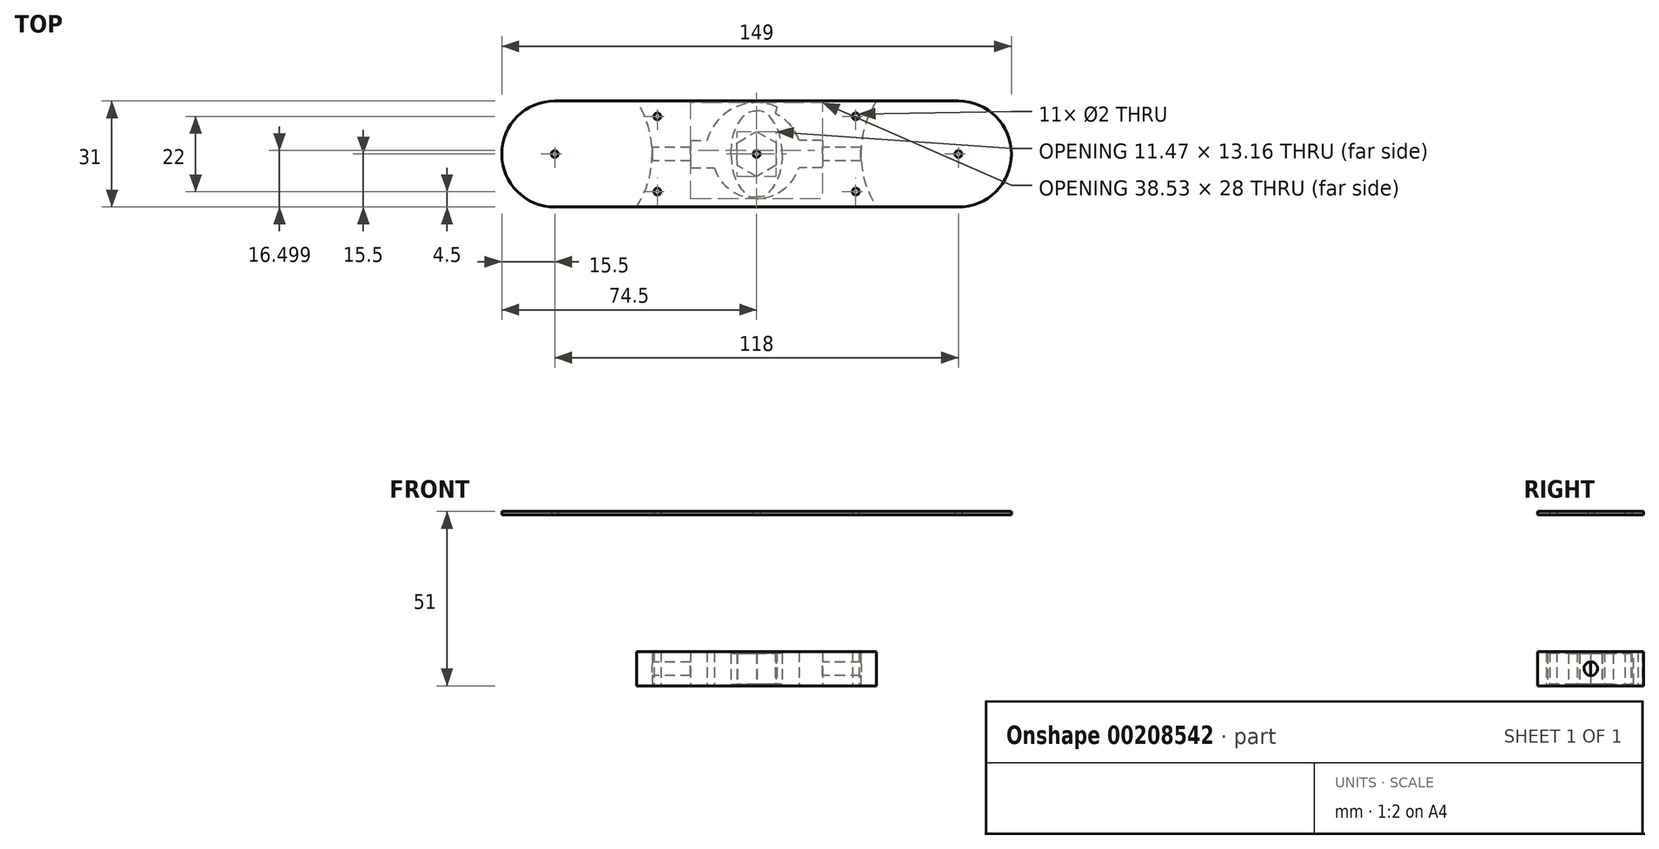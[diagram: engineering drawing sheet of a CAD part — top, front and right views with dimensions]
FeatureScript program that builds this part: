
annotation { "Feature Type Name" : "Feature", "Feature Type Description" : "" }
export const myFeature = defineFeature(function(context is Context, id is Id, definition is map)
    precondition{}
    {
        {
            var Q0;
            Q0=qCreatedBy(makeId("Top.planeOp"),FACE);
            var sketch = newSketch(context, id + "F0", { "sketchPlane" : qUnion([Q0])});
            skCircle(sketch, "E0", {"center": v(59, 0) * mm, "radius": 27.5 * mm});
            skCircle(sketch, "E1", {"center": v(-59, 0) * mm, "radius": 27.5 * mm});
            skCircle(sketch, "E2.0", {"center": v(59, 0) * mm, "radius": 28.5 * mm});
            skCircle(sketch, "E3.0", {"center": v(-59, 0) * mm, "radius": 28.5 * mm});
            skCircle(sketch, "E4", {"center": v(0, 0) * mm, "radius": 13 * mm});
            skCircle(sketch, "E5", {"center": v(59, 0) * mm, "radius": 15.5 * mm});
            skCircle(sketch, "E6", {"center": v(-59, 0) * mm, "radius": 15.5 * mm});
            skLineSegment(sketch, "E7", {"start": v(59.04, 15.5) * mm, "end": v(-59, 15.5) * mm});
            skLineSegment(sketch, "E8", {"start": v(-59.05, -15.5) * mm, "end": v(59, -15.5) * mm});
            skCircle(sketch, "E9", {"center": v(29, 11) * mm, "radius": 1 * mm});
            skCircle(sketch, "E10.MirrorC", {"center": v(-29, 11) * mm, "radius": 1 * mm});
            skCircle(sketch, "E11.MirrorC", {"center": v(29, -11) * mm, "radius": 1 * mm});
            skCircle(sketch, "E12.MirrorC", {"center": v(-29, -11) * mm, "radius": 1 * mm});
            skLineSegment(sketch, "E13.bottom", {"start": v(19.26, 4) * mm, "end": v(9.26, 4) * mm});
            skLineSegment(sketch, "E13.top", {"start": v(19.26, -4) * mm, "end": v(9.26, -4) * mm});
            skLineSegment(sketch, "E13.left", {"start": v(19.26, 4) * mm, "end": v(19.26, -4) * mm});
            skLineSegment(sketch, "E13.right", {"start": v(9.26, 4) * mm, "end": v(9.26, -4) * mm});
            skLineSegment(sketch, "E14.MirrorCS", {"start": v(-19.26, 4) * mm, "end": v(-19.26, -4) * mm});
            skLineSegment(sketch, "E15.MirrorCS", {"start": v(-19.26, 4) * mm, "end": v(-9.26, 4) * mm});
            skLineSegment(sketch, "E16.MirrorCS", {"start": v(-9.26, 4) * mm, "end": v(-9.26, -4) * mm});
            skLineSegment(sketch, "E17.MirrorCS", {"start": v(-19.26, -4) * mm, "end": v(-9.26, -4) * mm});
            skCircle(sketch, "E18.0", {"center": v(0, 0) * mm, "radius": 15 * mm});
            skLineSegment(sketch, "E19", {"start": v(5.95, 13.77) * mm, "end": v(5.43, 11.81) * mm});
            skCircle(sketch, "E20.cCircle", {"center": v(0, 0) * mm, "radius": 5.7 * mm, "construction": true});
            skLineSegment(sketch, "E20.0", {"start": v(-0.07, 6.58) * mm, "end": v(5.66, 3.35) * mm});
            skLineSegment(sketch, "E20.1", {"start": v(5.66, 3.35) * mm, "end": v(5.74, -3.23) * mm});
            skLineSegment(sketch, "E20.2", {"start": v(5.74, -3.23) * mm, "end": v(0.07, -6.58) * mm});
            skLineSegment(sketch, "E20.3", {"start": v(0.07, -6.58) * mm, "end": v(-5.66, -3.35) * mm});
            skLineSegment(sketch, "E20.4", {"start": v(-5.66, -3.35) * mm, "end": v(-5.74, 3.23) * mm});
            skLineSegment(sketch, "E20.5", {"start": v(-5.74, 3.23) * mm, "end": v(-0.07, 6.58) * mm});
            skPoint(sketch, "E20.0.midPoint", {"position": v(2.8, 4.97) * mm});
            skCircle(sketch, "E21", {"center": v(-59, 0) * mm, "radius": 1 * mm});
            skCircle(sketch, "E22", {"center": v(59, 0) * mm, "radius": 1 * mm});
            skCircle(sketch, "E23", {"center": v(0, 0) * mm, "radius": 1 * mm});
            skLineSegment(sketch, "E24", {"start": v(-73.26, 28.93) * mm, "end": v(99.1, 13.06) * mm});
            skLineSegment(sketch, "E25", {"start": v(-95.04, -13.9) * mm, "end": v(98.15, -31.1) * mm});
            skLineSegment(sketch, "E26", {"start": v(32.84, 0) * mm, "end": v(29.84, 0) * mm});
            skLineSegment(sketch, "E27.1.0", {"start": v(33.37, -5.27) * mm, "end": v(30.43, -5.87) * mm});
            skLineSegment(sketch, "E27.2.0", {"start": v(34.96, -10.32) * mm, "end": v(32.2, -11.5) * mm});
            skLineSegment(sketch, "E28.2.3.0", {"start": v(37.53, -14.95) * mm, "end": v(35.06, -16.66) * mm});
            skLineSegment(sketch, "E28.2.4.0", {"start": v(40.97, -18.96) * mm, "end": v(38.9, -21.14) * mm});
            skLineSegment(sketch, "E28.2.5.0", {"start": v(45.16, -22.2) * mm, "end": v(43.57, -24.75) * mm});
            skLineSegment(sketch, "E28.2.6.0", {"start": v(49.91, -24.53) * mm, "end": v(48.87, -27.35) * mm});
            skLineSegment(sketch, "E28.2.7.0", {"start": v(55.04, -25.86) * mm, "end": v(54.58, -28.83) * mm});
            skLineSegment(sketch, "E28.2.8.0", {"start": v(60.33, -26.13) * mm, "end": v(60.48, -29.13) * mm});
            skLineSegment(sketch, "E28.2.9.0", {"start": v(65.56, -25.33) * mm, "end": v(66.3, -28.23) * mm});
            skLineSegment(sketch, "E28.2.10.0", {"start": v(70.52, -23.49) * mm, "end": v(71.84, -26.18) * mm});
            skLineSegment(sketch, "E28.2.11.0", {"start": v(75.01, -20.69) * mm, "end": v(76.85, -23.06) * mm});
            skLineSegment(sketch, "E28.2.12.0", {"start": v(78.85, -17.04) * mm, "end": v(81.13, -19) * mm});
            skLineSegment(sketch, "E28.2.13.0", {"start": v(81.88, -12.7) * mm, "end": v(84.5, -14.15) * mm});
            skLineSegment(sketch, "E28.2.14.0", {"start": v(83.96, -7.83) * mm, "end": v(86.83, -8.73) * mm});
            skLineSegment(sketch, "E28.2.15.0", {"start": v(85.03, -2.65) * mm, "end": v(88.01, -2.95) * mm});
            skLineSegment(sketch, "E28.2.16.0", {"start": v(85.03, 2.65) * mm, "end": v(88.01, 2.95) * mm});
            skLineSegment(sketch, "E28.2.17.0", {"start": v(83.96, 7.83) * mm, "end": v(86.83, 8.73) * mm});
            skLineSegment(sketch, "E28.2.18.0", {"start": v(81.88, 12.7) * mm, "end": v(84.5, 14.15) * mm});
            skLineSegment(sketch, "E28.2.19.0", {"start": v(78.85, 17.04) * mm, "end": v(81.13, 19) * mm});
            skLineSegment(sketch, "E28.2.20.0", {"start": v(75.01, 20.69) * mm, "end": v(76.85, 23.06) * mm});
            skLineSegment(sketch, "E28.2.21.0", {"start": v(70.52, 23.49) * mm, "end": v(71.84, 26.18) * mm});
            skLineSegment(sketch, "E28.2.22.0", {"start": v(65.56, 25.33) * mm, "end": v(66.3, 28.23) * mm});
            skLineSegment(sketch, "E28.2.23.0", {"start": v(60.33, 26.13) * mm, "end": v(60.48, 29.13) * mm});
            skLineSegment(sketch, "E28.2.24.0", {"start": v(55.04, 25.86) * mm, "end": v(54.58, 28.83) * mm});
            skLineSegment(sketch, "E28.2.25.0", {"start": v(49.91, 24.53) * mm, "end": v(48.87, 27.35) * mm});
            skLineSegment(sketch, "E28.2.26.0", {"start": v(45.16, 22.2) * mm, "end": v(43.57, 24.75) * mm});
            skLineSegment(sketch, "E28.2.27.0", {"start": v(40.97, 18.96) * mm, "end": v(38.9, 21.14) * mm});
            skLineSegment(sketch, "E29", {"start": v(-33.37, 0) * mm, "end": v(-30.37, 0) * mm});
            skLineSegment(sketch, "E30.1.0", {"start": v(-33.9, 5.16) * mm, "end": v(-30.95, 5.76) * mm});
            skLineSegment(sketch, "E30.2.0", {"start": v(-35.44, 10.1) * mm, "end": v(-32.69, 11.3) * mm});
            skLineSegment(sketch, "E31.1.3.0", {"start": v(-37.96, 14.64) * mm, "end": v(-35.5, 16.36) * mm});
            skLineSegment(sketch, "E31.1.4.0", {"start": v(-41.34, 18.58) * mm, "end": v(-39.27, 20.75) * mm});
            skLineSegment(sketch, "E31.1.5.0", {"start": v(-45.44, 21.75) * mm, "end": v(-43.85, 24.3) * mm});
            skLineSegment(sketch, "E31.1.6.0", {"start": v(-50.1, 24.04) * mm, "end": v(-49.06, 26.85) * mm});
            skLineSegment(sketch, "E31.1.7.0", {"start": v(-55.12, 25.34) * mm, "end": v(-54.66, 28.3) * mm});
            skLineSegment(sketch, "E31.1.8.0", {"start": v(-60.3, 25.6) * mm, "end": v(-60.45, 28.6) * mm});
            skLineSegment(sketch, "E31.1.9.0", {"start": v(-65.43, 24.81) * mm, "end": v(-66.18, 27.72) * mm});
            skLineSegment(sketch, "E31.1.10.0", {"start": v(-70.29, 23.01) * mm, "end": v(-71.6, 25.7) * mm});
            skLineSegment(sketch, "E31.1.11.0", {"start": v(-74.7, 20.27) * mm, "end": v(-76.53, 22.64) * mm});
            skLineSegment(sketch, "E31.1.12.0", {"start": v(-78.45, 16.7) * mm, "end": v(-80.73, 18.65) * mm});
            skLineSegment(sketch, "E31.1.13.0", {"start": v(-81.41, 12.44) * mm, "end": v(-84.04, 13.9) * mm});
            skLineSegment(sketch, "E31.1.14.0", {"start": v(-83.46, 7.67) * mm, "end": v(-86.32, 8.57) * mm});
            skLineSegment(sketch, "E31.1.15.0", {"start": v(-84.5, 2.6) * mm, "end": v(-87.49, 2.9) * mm});
            skLineSegment(sketch, "E31.1.16.0", {"start": v(-84.5, -2.6) * mm, "end": v(-87.49, -2.9) * mm});
            skLineSegment(sketch, "E31.1.17.0", {"start": v(-83.46, -7.67) * mm, "end": v(-86.32, -8.57) * mm});
            skLineSegment(sketch, "E31.1.18.0", {"start": v(-81.41, -12.44) * mm, "end": v(-84.04, -13.9) * mm});
            skLineSegment(sketch, "E31.1.19.0", {"start": v(-78.45, -16.7) * mm, "end": v(-80.73, -18.65) * mm});
            skLineSegment(sketch, "E31.1.20.0", {"start": v(-74.7, -20.27) * mm, "end": v(-76.53, -22.64) * mm});
            skLineSegment(sketch, "E31.1.21.0", {"start": v(-70.29, -23.01) * mm, "end": v(-71.6, -25.7) * mm});
            skLineSegment(sketch, "E31.1.22.0", {"start": v(-65.43, -24.81) * mm, "end": v(-66.18, -27.72) * mm});
            skLineSegment(sketch, "E31.1.23.0", {"start": v(-60.3, -25.6) * mm, "end": v(-60.45, -28.6) * mm});
            skLineSegment(sketch, "E31.1.24.0", {"start": v(-55.12, -25.34) * mm, "end": v(-54.66, -28.3) * mm});
            skLineSegment(sketch, "E31.1.25.0", {"start": v(-50.1, -24.04) * mm, "end": v(-49.06, -26.85) * mm});
            skLineSegment(sketch, "E31.1.26.0", {"start": v(-45.44, -21.75) * mm, "end": v(-43.85, -24.3) * mm});
            skLineSegment(sketch, "E31.1.27.0", {"start": v(-41.34, -18.58) * mm, "end": v(-39.27, -20.75) * mm});
            skLineSegment(sketch, "E32.2.28.0", {"start": v(37.53, 14.95) * mm, "end": v(35.06, 16.66) * mm});
            skLineSegment(sketch, "E32.2.29.0", {"start": v(34.96, 10.32) * mm, "end": v(32.2, 11.5) * mm});
            skLineSegment(sketch, "E32.2.30.0", {"start": v(33.37, 5.27) * mm, "end": v(30.43, 5.87) * mm});
            skLineSegment(sketch, "E33.1.28.0", {"start": v(-37.96, -14.64) * mm, "end": v(-35.5, -16.36) * mm});
            skLineSegment(sketch, "E33.1.29.0", {"start": v(-35.44, -10.1) * mm, "end": v(-32.69, -11.3) * mm});
            skLineSegment(sketch, "E33.1.30.0", {"start": v(-33.9, -5.16) * mm, "end": v(-30.95, -5.76) * mm});
            skFitSpline(sketch, "E34", {"points": [v(7.5, 0) * mm, v(-7.5, 0) * mm], "startDerivative": vector(-15, 0) * mm, "endDerivative": vector(-15, 0) * mm});
            skFitSpline(sketch, "E35", {"points": [v(7.5, 0) * mm, v(5.66, 8.22) * mm, v(2.54, 12.14) * mm, v(0, 12.58) * mm], "startDerivative": vector(-1.7, 31.98) * mm, "endDerivative": vector(-10.69, 0) * mm});
            skFitSpline(sketch, "E36.MirrorCS", {"points": [v(7.5, 0) * mm, v(5.66, -8.22) * mm, v(2.54, -12.14) * mm, v(0, -12.58) * mm], "startDerivative": vector(-1.7, -31.98) * mm, "endDerivative": vector(-10.69, 0) * mm});
            skFitSpline(sketch, "E37.MirrorCS", {"points": [v(-7.5, 0) * mm, v(-5.66, 8.22) * mm, v(-2.54, 12.14) * mm, v(0, 12.58) * mm], "startDerivative": vector(1.7, 31.98) * mm, "endDerivative": vector(10.69, 0) * mm});
            skFitSpline(sketch, "E38.MirrorCS", {"points": [v(-7.5, 0) * mm, v(-5.66, -8.22) * mm, v(-2.54, -12.14) * mm, v(0, -12.58) * mm], "startDerivative": vector(1.7, -31.98) * mm, "endDerivative": vector(10.69, 0) * mm});
            skSolve(sketch);
        }
        {
            var Q0;
            Q0=makeQuery(id+"F0.imprint","IMPRINT",FACE,{"disambiguationData":[TD([[makeQuery(id+"F0.imprint","IMPRINT",EDGE,{"derivedFrom":sQuery(id+"F0.wireOp",EDGE,"E9")}),-1.0]])]});
            var Q1;
            {var subQ0=sQuery(id+"F0.wireOp",EDGE,"E19");Q1=makeQuery(id+"F0.imprint","IMPRINT",FACE,{"disambiguationData":[TD([[makeQuery(id+"F0.imprint","IMPRINT",EDGE,{"derivedFrom":subQ0}),1.0]])]});}
            var Q2;
            {var subQ0=sQuery(id+"F0.wireOp",EDGE,"E17.MirrorCS");var subQ1=sQuery(id+"F0.wireOp",EDGE,"E4");var subQ2=makeQuery(id+"F0.imprint","INTERSECT",VERTEX,{"derivedFrom":[subQ1,subQ0]});Q2=makeQuery(id+"F0.imprint","IMPRINT",FACE,{"disambiguationData":[TD([[makeQuery(id+"F0.imprint","IMPRINT",EDGE,{"disambiguationData":[TD([[subQ2,-1.0]])],"derivedFrom":subQ1}),-1.0]])]});}
            extrude(context, id + "F1", {"entities" : qUnion([Q0, Q1, Q2]), "flatOperationType" : FlatOperationType.REMOVE, "offsetDistance" : 25 * mm, "depth" : 10 * mm, "domain" : OperationDomain.MODEL, "symmetric" : true});
        }
        {
            var Q0;
            Q0=qCreatedBy(makeId("Right.planeOp"),FACE);
            var sketch = newSketch(context, id + "F2", { "sketchPlane" : qUnion([Q0])});
            skCircle(sketch, "E39", {"center": v(0, 0) * mm, "radius": 2 * mm});
            skSolve(sketch);
        }
        {
            var Q0;
            Q0=makeQuery(id+"F2.imprint","IMPRINT",FACE,{"disambiguationData":[TD([[makeQuery(id+"F2.imprint","IMPRINT",EDGE,{"derivedFrom":sQuery(id+"F2.wireOp",EDGE,"E39")}),1.0]])]});
            extrude(context, id + "F3", {"entities" : qUnion([Q0]), "operationType" : NewBodyOperationType.REMOVE, "depth" : 200 * mm, "symmetric" : true});
        }
        {
            var Q0;
            {var subQ0=sQuery(id+"F0.wireOp",EDGE,"E20.2");Q0=makeQuery(id+"F0.imprint","IMPRINT",FACE,{"disambiguationData":[TD([[makeQuery(id+"F0.imprint","IMPRINT",EDGE,{"derivedFrom":subQ0}),1.0]])]});}
            var Q1;
            {var subQ0=sQuery(id+"F0.wireOp",EDGE,"6NjTobdY-lf3O-SfGc-2mSh-fdBj5DLjCS89");Q1=makeQuery(id+"F0.imprint","IMPRINT",FACE,{"disambiguationData":[TD([[makeQuery(id+"F0.imprint","IMPRINT",EDGE,{"derivedFrom":subQ0}),-1.0]])]});}
            var Q2;
            {var subQ4=sQuery(id+"F0.wireOp",EDGE,"E20.0");Q2=makeQuery(id+"F0.imprint","IMPRINT",FACE,{"disambiguationData":[TD([[makeQuery(id+"F0.imprint","IMPRINT",EDGE,{"derivedFrom":subQ4}),1.0]])]});}
            var Q3;
            {var subQ0=sQuery(id+"F0.wireOp",EDGE,"725a75dc-4944-4634-ad2c-78751c0e6b120.MirrorCS");Q3=makeQuery(id+"F0.imprint","IMPRINT",FACE,{"disambiguationData":[TD([[makeQuery(id+"F0.imprint","IMPRINT",EDGE,{"derivedFrom":subQ0}),1.0]])]});}
            extrude(context, id + "F4", {"entities" : qUnion([Q0, Q1, Q2, Q3]), "depth" : 9 * mm, "symmetric" : true});
        }
        {
            var Q0;
            Q0=makeQuery(id+"F0.imprint","IMPRINT",FACE,{"disambiguationData":[TD([[makeQuery(id+"F0.imprint","IMPRINT",EDGE,{"derivedFrom":sQuery(id+"F0.wireOp",EDGE,"E21")}),-1.0]])]});
            var Q1;
            {var subQ0=sQuery(id+"F0.wireOp",EDGE,"E7");var subQ1=sQuery(id+"F0.wireOp",EDGE,"E1");var subQ2=makeQuery(id+"F0.imprint","INTERSECT",VERTEX,{"derivedFrom":[subQ1,subQ0]});Q1=makeQuery(id+"F0.imprint","IMPRINT",FACE,{"disambiguationData":[TD([[makeQuery(id+"F0.imprint","IMPRINT",EDGE,{"disambiguationData":[TD([[subQ2,1.0]])],"derivedFrom":subQ1}),1.0]])]});}
            var Q2;
            {var subQ0=sQuery(id+"F0.wireOp",EDGE,"E7");var subQ1=sQuery(id+"F0.wireOp",EDGE,"E1");var subQ2=makeQuery(id+"F0.imprint","INTERSECT",VERTEX,{"derivedFrom":[subQ1,subQ0]});Q2=makeQuery(id+"F0.imprint","IMPRINT",FACE,{"disambiguationData":[TD([[makeQuery(id+"F0.imprint","IMPRINT",EDGE,{"disambiguationData":[TD([[subQ2,1.0]])],"derivedFrom":subQ1}),-1.0]])]});}
            var Q3;
            Q3=makeQuery(id+"F0.imprint","IMPRINT",FACE,{"disambiguationData":[TD([[makeQuery(id+"F0.imprint","IMPRINT",EDGE,{"derivedFrom":sQuery(id+"F0.wireOp",EDGE,"E9")}),-1.0]])]});
            var Q4;
            {var subQ0=sQuery(id+"F0.wireOp",EDGE,"E7");var subQ1=sQuery(id+"F0.wireOp",EDGE,"E0");var subQ2=makeQuery(id+"F0.imprint","INTERSECT",VERTEX,{"derivedFrom":[subQ1,subQ0]});Q4=makeQuery(id+"F0.imprint","IMPRINT",FACE,{"disambiguationData":[TD([[makeQuery(id+"F0.imprint","IMPRINT",EDGE,{"disambiguationData":[TD([[subQ2,-1.0]])],"derivedFrom":subQ1}),1.0]])]});}
            var Q5;
            Q5=makeQuery(id+"F0.imprint","IMPRINT",FACE,{"disambiguationData":[TD([[makeQuery(id+"F0.imprint","IMPRINT",EDGE,{"derivedFrom":sQuery(id+"F0.wireOp",EDGE,"E22")}),-1.0]])]});
            var Q6;
            {var subQ0=sQuery(id+"F0.wireOp",EDGE,"E13.left");Q6=makeQuery(id+"F0.imprint","IMPRINT",FACE,{"disambiguationData":[TD([[makeQuery(id+"F0.imprint","IMPRINT",EDGE,{"derivedFrom":subQ0}),-1.0]])]});}
            var Q7;
            {var subQ0=sQuery(id+"F0.wireOp",EDGE,"E13.bottom");var subQ1=sQuery(id+"F0.wireOp",EDGE,"E4");var subQ2=makeQuery(id+"F0.imprint","INTERSECT",VERTEX,{"derivedFrom":[subQ1,subQ0]});Q7=makeQuery(id+"F0.imprint","IMPRINT",FACE,{"disambiguationData":[TD([[makeQuery(id+"F0.imprint","IMPRINT",EDGE,{"disambiguationData":[TD([[subQ2,1.0]])],"derivedFrom":subQ1}),-1.0]])]});}
            var Q8;
            {var subQ0=sQuery(id+"F0.wireOp",EDGE,"E19");Q8=makeQuery(id+"F0.imprint","IMPRINT",FACE,{"disambiguationData":[TD([[makeQuery(id+"F0.imprint","IMPRINT",EDGE,{"derivedFrom":subQ0}),1.0]])]});}
            var Q9;
            {var subQ0=sQuery(id+"F0.wireOp",EDGE,"E17.MirrorCS");var subQ1=sQuery(id+"F0.wireOp",EDGE,"E4");var subQ2=makeQuery(id+"F0.imprint","INTERSECT",VERTEX,{"derivedFrom":[subQ1,subQ0]});Q9=makeQuery(id+"F0.imprint","IMPRINT",FACE,{"disambiguationData":[TD([[makeQuery(id+"F0.imprint","IMPRINT",EDGE,{"disambiguationData":[TD([[subQ2,-1.0]])],"derivedFrom":subQ1}),-1.0]])]});}
            var Q10;
            {var subQ0=sQuery(id+"F0.wireOp",EDGE,"E14.MirrorCS");Q10=makeQuery(id+"F0.imprint","IMPRINT",FACE,{"disambiguationData":[TD([[makeQuery(id+"F0.imprint","IMPRINT",EDGE,{"derivedFrom":subQ0}),1.0]])]});}
            var Q11;
            {var subQ0=sQuery(id+"F0.wireOp",EDGE,"E15.MirrorCS");var subQ1=sQuery(id+"F0.wireOp",EDGE,"E4");var subQ2=makeQuery(id+"F0.imprint","INTERSECT",VERTEX,{"derivedFrom":[subQ1,subQ0]});Q11=makeQuery(id+"F0.imprint","IMPRINT",FACE,{"disambiguationData":[TD([[makeQuery(id+"F0.imprint","IMPRINT",EDGE,{"disambiguationData":[TD([[subQ2,-1.0]])],"derivedFrom":subQ1}),-1.0]])]});}
            var Q12;
            {var subQ0=sQuery(id+"F0.wireOp",EDGE,"E19");Q12=makeQuery(id+"F0.imprint","IMPRINT",FACE,{"disambiguationData":[TD([[makeQuery(id+"F0.imprint","IMPRINT",EDGE,{"derivedFrom":subQ0}),-1.0]])]});}
            var Q13;
            {var subQ4=sQuery(id+"F0.wireOp",EDGE,"E13.right");Q13=makeQuery(id+"F0.imprint","IMPRINT",FACE,{"disambiguationData":[TD([[makeQuery(id+"F0.imprint","IMPRINT",EDGE,{"derivedFrom":subQ4}),-1.0]])]});}
            var Q14;
            {var subQ5=sQuery(id+"F0.wireOp",EDGE,"E13.right");Q14=makeQuery(id+"F0.imprint","IMPRINT",FACE,{"disambiguationData":[TD([[makeQuery(id+"F0.imprint","IMPRINT",EDGE,{"derivedFrom":subQ5}),1.0]])]});}
            var Q15;
            {var subQ5=sQuery(id+"F0.wireOp",EDGE,"E16.MirrorCS");Q15=makeQuery(id+"F0.imprint","IMPRINT",FACE,{"disambiguationData":[TD([[makeQuery(id+"F0.imprint","IMPRINT",EDGE,{"derivedFrom":subQ5}),-1.0]])]});}
            var Q16;
            {var subQ4=sQuery(id+"F0.wireOp",EDGE,"E20.0");Q16=makeQuery(id+"F0.imprint","IMPRINT",FACE,{"disambiguationData":[TD([[makeQuery(id+"F0.imprint","IMPRINT",EDGE,{"derivedFrom":subQ4}),1.0]])]});}
            var Q17;
            {var subQ0=sQuery(id+"F0.wireOp",EDGE,"E20.2");Q17=makeQuery(id+"F0.imprint","IMPRINT",FACE,{"disambiguationData":[TD([[makeQuery(id+"F0.imprint","IMPRINT",EDGE,{"derivedFrom":subQ0}),1.0]])]});}
            var Q18;
            {var subQ0=sQuery(id+"F0.wireOp",EDGE,"6NjTobdY-lf3O-SfGc-2mSh-fdBj5DLjCS89");Q18=makeQuery(id+"F0.imprint","IMPRINT",FACE,{"disambiguationData":[TD([[makeQuery(id+"F0.imprint","IMPRINT",EDGE,{"derivedFrom":subQ0}),-1.0]])]});}
            var Q19;
            {var subQ0=sQuery(id+"F0.wireOp",EDGE,"725a75dc-4944-4634-ad2c-78751c0e6b120.MirrorCS");Q19=makeQuery(id+"F0.imprint","IMPRINT",FACE,{"disambiguationData":[TD([[makeQuery(id+"F0.imprint","IMPRINT",EDGE,{"derivedFrom":subQ0}),1.0]])]});}
            var Q20;
            {var subQ5=sQuery(id+"F0.wireOp",EDGE,"E20.2");Q20=makeQuery(id+"F0.imprint","IMPRINT",FACE,{"disambiguationData":[TD([[makeQuery(id+"F0.imprint","IMPRINT",EDGE,{"derivedFrom":subQ5}),-1.0]])]});}
            var Q21;
            Q21=makeQuery(id+"F0.imprint","IMPRINT",FACE,{"disambiguationData":[TD([[makeQuery(id+"F0.imprint","IMPRINT",EDGE,{"derivedFrom":sQuery(id+"F0.wireOp",EDGE,"E23")}),-1.0]])]});
            var Q22;
            {var subQ0=sQuery(id+"F0.wireOp",EDGE,"E20.0");Q22=makeQuery(id+"F0.imprint","IMPRINT",FACE,{"disambiguationData":[TD([[makeQuery(id+"F0.imprint","IMPRINT",EDGE,{"derivedFrom":subQ0}),-1.0]])]});}
            var Q23;
            {var subQ0=sQuery(id+"F0.wireOp",EDGE,"E7");var subQ1=sQuery(id+"F0.wireOp",EDGE,"E0");var subQ2=makeQuery(id+"F0.imprint","INTERSECT",VERTEX,{"derivedFrom":[subQ1,subQ0]});Q23=makeQuery(id+"F0.imprint","IMPRINT",FACE,{"disambiguationData":[TD([[makeQuery(id+"F0.imprint","IMPRINT",EDGE,{"disambiguationData":[TD([[subQ2,-1.0]])],"derivedFrom":subQ1}),-1.0]])]});}
            var Q24;
            {var subQ0=sQuery(id+"F0.wireOp",EDGE,"E26");var subQ1=sQuery(id+"F0.wireOp",EDGE,"E0");var subQ2=makeQuery(id+"F0.imprint","INTERSECT",VERTEX,{"derivedFrom":[subQ1,subQ0]});Q24=makeQuery(id+"F0.imprint","IMPRINT",FACE,{"disambiguationData":[TD([[makeQuery(id+"F0.imprint","IMPRINT",EDGE,{"disambiguationData":[TD([[subQ2,-1.0]])],"derivedFrom":subQ1}),-1.0]])]});}
            var Q25;
            {var subQ0=sQuery(id+"F0.wireOp",EDGE,"E27.1.0");var subQ1=sQuery(id+"F0.wireOp",EDGE,"E0");var subQ2=makeQuery(id+"F0.imprint","INTERSECT",VERTEX,{"derivedFrom":[subQ1,subQ0]});Q25=makeQuery(id+"F0.imprint","IMPRINT",FACE,{"disambiguationData":[TD([[makeQuery(id+"F0.imprint","IMPRINT",EDGE,{"disambiguationData":[TD([[subQ2,-1.0]])],"derivedFrom":subQ1}),-1.0]])]});}
            var Q26;
            {var subQ0=sQuery(id+"F0.wireOp",EDGE,"E27.2.0");var subQ1=sQuery(id+"F0.wireOp",EDGE,"E0");var subQ2=makeQuery(id+"F0.imprint","INTERSECT",VERTEX,{"derivedFrom":[subQ1,subQ0]});Q26=makeQuery(id+"F0.imprint","IMPRINT",FACE,{"disambiguationData":[TD([[makeQuery(id+"F0.imprint","IMPRINT",EDGE,{"disambiguationData":[TD([[subQ2,-1.0]])],"derivedFrom":subQ1}),-1.0]])]});}
            var Q27;
            {var subQ0=sQuery(id+"F0.wireOp",EDGE,"E32.2.29.0");var subQ1=sQuery(id+"F0.wireOp",EDGE,"E0");var subQ2=makeQuery(id+"F0.imprint","INTERSECT",VERTEX,{"derivedFrom":[subQ1,subQ0]});Q27=makeQuery(id+"F0.imprint","IMPRINT",FACE,{"disambiguationData":[TD([[makeQuery(id+"F0.imprint","IMPRINT",EDGE,{"disambiguationData":[TD([[subQ2,-1.0]])],"derivedFrom":subQ1}),-1.0]])]});}
            var Q28;
            {var subQ0=sQuery(id+"F0.wireOp",EDGE,"E32.2.30.0");var subQ1=sQuery(id+"F0.wireOp",EDGE,"E0");var subQ2=makeQuery(id+"F0.imprint","INTERSECT",VERTEX,{"derivedFrom":[subQ1,subQ0]});Q28=makeQuery(id+"F0.imprint","IMPRINT",FACE,{"disambiguationData":[TD([[makeQuery(id+"F0.imprint","IMPRINT",EDGE,{"disambiguationData":[TD([[subQ2,-1.0]])],"derivedFrom":subQ1}),-1.0]])]});}
            var Q29;
            {var subQ0=sQuery(id+"F0.wireOp",EDGE,"E30.1.0");var subQ1=sQuery(id+"F0.wireOp",EDGE,"E1");var subQ2=makeQuery(id+"F0.imprint","INTERSECT",VERTEX,{"derivedFrom":[subQ1,subQ0]});Q29=makeQuery(id+"F0.imprint","IMPRINT",FACE,{"disambiguationData":[TD([[makeQuery(id+"F0.imprint","IMPRINT",EDGE,{"disambiguationData":[TD([[subQ2,-1.0]])],"derivedFrom":subQ1}),-1.0]])]});}
            var Q30;
            {var subQ0=sQuery(id+"F0.wireOp",EDGE,"E30.1.0");var subQ1=sQuery(id+"F0.wireOp",EDGE,"E1");var subQ2=makeQuery(id+"F0.imprint","INTERSECT",VERTEX,{"derivedFrom":[subQ1,subQ0]});Q30=makeQuery(id+"F0.imprint","IMPRINT",FACE,{"disambiguationData":[TD([[makeQuery(id+"F0.imprint","IMPRINT",EDGE,{"disambiguationData":[TD([[subQ2,1.0]])],"derivedFrom":subQ1}),-1.0]])]});}
            var Q31;
            {var subQ0=sQuery(id+"F0.wireOp",EDGE,"E29");var subQ1=sQuery(id+"F0.wireOp",EDGE,"E1");var subQ2=makeQuery(id+"F0.imprint","INTERSECT",VERTEX,{"derivedFrom":[subQ1,subQ0]});Q31=makeQuery(id+"F0.imprint","IMPRINT",FACE,{"disambiguationData":[TD([[makeQuery(id+"F0.imprint","IMPRINT",EDGE,{"disambiguationData":[TD([[subQ2,1.0]])],"derivedFrom":subQ1}),-1.0]])]});}
            var Q32;
            {var subQ0=sQuery(id+"F0.wireOp",EDGE,"E33.1.29.0");var subQ1=sQuery(id+"F0.wireOp",EDGE,"E1");var subQ2=makeQuery(id+"F0.imprint","INTERSECT",VERTEX,{"derivedFrom":[subQ1,subQ0]});Q32=makeQuery(id+"F0.imprint","IMPRINT",FACE,{"disambiguationData":[TD([[makeQuery(id+"F0.imprint","IMPRINT",EDGE,{"disambiguationData":[TD([[subQ2,-1.0]])],"derivedFrom":subQ1}),-1.0]])]});}
            var Q33;
            {var subQ0=sQuery(id+"F0.wireOp",EDGE,"E33.1.29.0");var subQ1=sQuery(id+"F0.wireOp",EDGE,"E1");var subQ2=makeQuery(id+"F0.imprint","INTERSECT",VERTEX,{"derivedFrom":[subQ1,subQ0]});Q33=makeQuery(id+"F0.imprint","IMPRINT",FACE,{"disambiguationData":[TD([[makeQuery(id+"F0.imprint","IMPRINT",EDGE,{"disambiguationData":[TD([[subQ2,1.0]])],"derivedFrom":subQ1}),-1.0]])]});}
            extrude(context, id + "F5", {"entities" : qUnion([Q0, Q1, Q2, Q3, Q4, Q5, Q6, Q7, Q8, Q9, Q10, Q11, Q12, Q13, Q14, Q15, Q16, Q17, Q18, Q19, Q20, Q21, Q22, Q23, Q24, Q25, Q26, Q27, Q28, Q29, Q30, Q31, Q32, Q33]), "depth" : 46 * mm, "hasSecondDirection" : true, "secondDirectionOppositeDirection" : false, "secondDirectionDepth" : 45 * mm});
        }
    });
